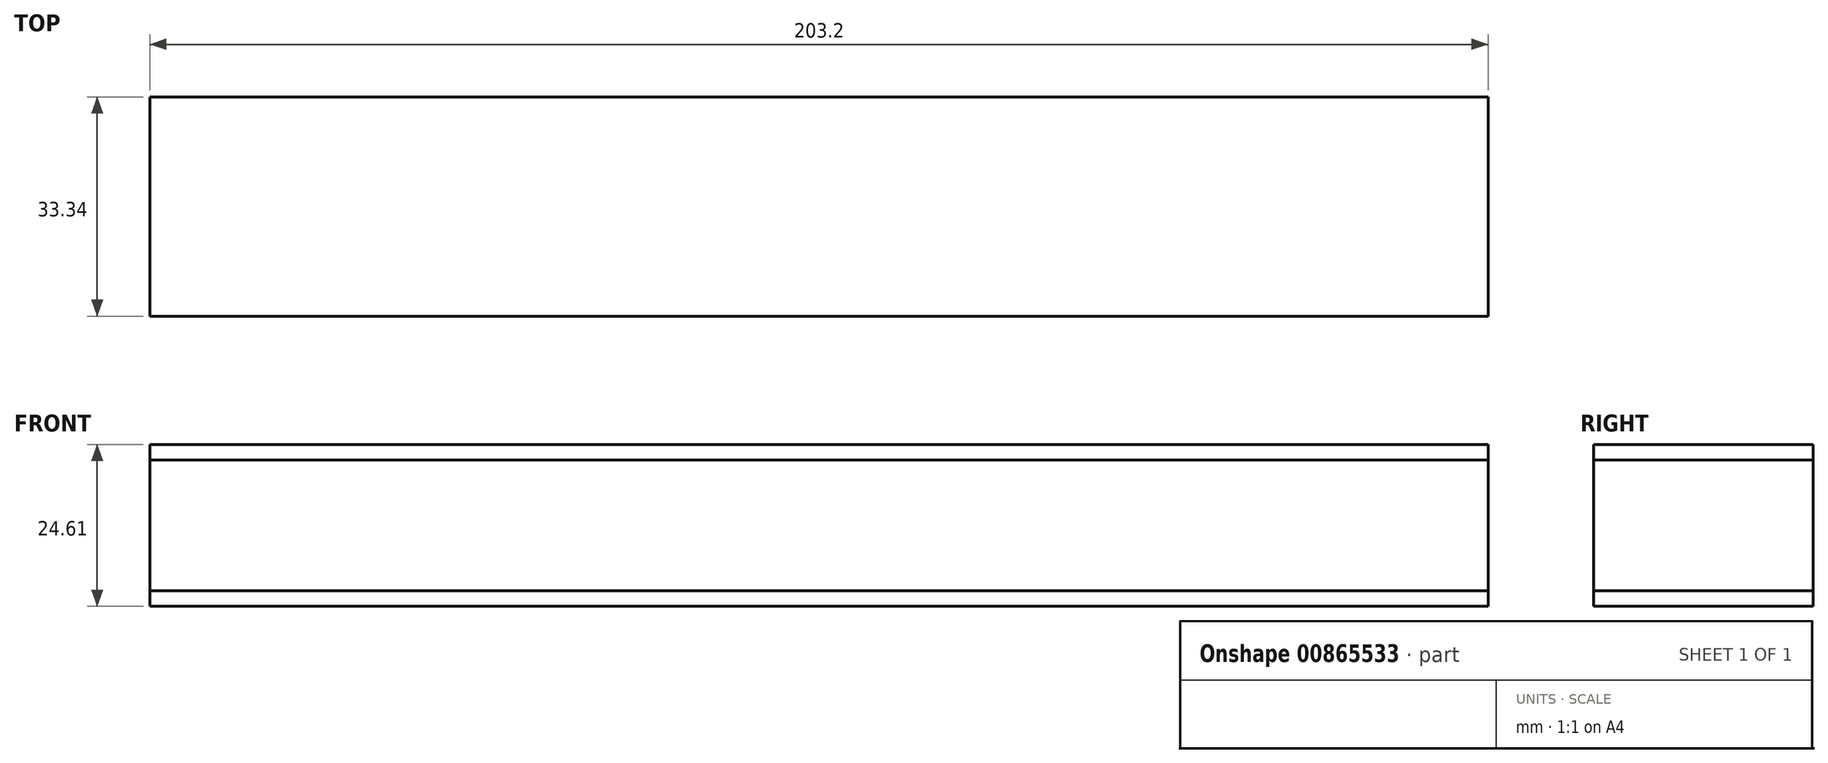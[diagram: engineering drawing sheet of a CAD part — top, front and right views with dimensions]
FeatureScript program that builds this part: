
annotation { "Feature Type Name" : "Feature", "Feature Type Description" : "" }
export const myFeature = defineFeature(function(context is Context, id is Id, definition is map)
    precondition{}
    {
        {
            var Q0;
            Q0=qCreatedBy(makeId("Front.planeOp"),FACE);
            var sketch = newSketch(context, id + "F0", { "sketchPlane" : qUnion([Q0])});
            skLineSegment(sketch, "E0.bottom", {"start": v(0, 0) * mm, "end": v(203.2, 0) * mm});
            skLineSegment(sketch, "E0.top", {"start": v(0, 19.84) * mm, "end": v(203.2, 19.84) * mm});
            skLineSegment(sketch, "E0.left", {"start": v(0, 0) * mm, "end": v(0, 19.84) * mm});
            skLineSegment(sketch, "E0.right", {"start": v(203.2, 0) * mm, "end": v(203.2, 19.84) * mm});
            skSolve(sketch);
        }
        {
            var Q0;
            Q0=makeQuery(id+"F0.imprint","IMPRINT",FACE,{"disambiguationData":[TD([[makeQuery(id+"F0.imprint","IMPRINT",EDGE,{"derivedFrom":sQuery(id+"F0.wireOp",EDGE,"E0.top")}),-1.0]])]});
            extrude(context, id + "F1", {"entities" : qUnion([Q0]), "depth" : 33.34 * mm, "offsetDistance" : 25.4 * mm});
        }
        {
            var Q0;
            Q0=qCreatedBy(makeId("Front.planeOp"),FACE);
            var sketch = newSketch(context, id + "F2", { "sketchPlane" : qUnion([Q0])});
            skLineSegment(sketch, "E1.bottom", {"start": v(0, 19.84) * mm, "end": v(203.2, 19.84) * mm});
            skLineSegment(sketch, "E1.top", {"start": v(0, 22.23) * mm, "end": v(203.2, 22.23) * mm});
            skLineSegment(sketch, "E1.left", {"start": v(0, 19.84) * mm, "end": v(0, 22.23) * mm});
            skLineSegment(sketch, "E1.right", {"start": v(203.2, 19.84) * mm, "end": v(203.2, 22.23) * mm});
            skLineSegment(sketch, "E2", {"start": v(0, 9.92) * mm, "end": v(203.53, 9.92) * mm, "construction": true});
            skLineSegment(sketch, "E3.MirrorCS", {"start": v(0, 0) * mm, "end": v(203.2, 0) * mm});
            skLineSegment(sketch, "E4.MirrorCS", {"start": v(0, -2.38) * mm, "end": v(203.2, -2.38) * mm});
            skLineSegment(sketch, "E5.MirrorCS", {"start": v(0, 0) * mm, "end": v(0, -2.38) * mm});
            skLineSegment(sketch, "E6.MirrorCS", {"start": v(203.2, 0) * mm, "end": v(203.2, -2.38) * mm});
            skSolve(sketch);
        }
        {
            var Q0;
            Q0=makeQuery(id+"F2.imprint","IMPRINT",FACE,{"disambiguationData":[TD([[makeQuery(id+"F2.imprint","IMPRINT",EDGE,{"derivedFrom":sQuery(id+"F2.wireOp",EDGE,"E1.bottom")}),1.0]])]});
            var Q1;
            Q1=makeQuery(id+"F2.imprint","IMPRINT",FACE,{"disambiguationData":[TD([[makeQuery(id+"F2.imprint","IMPRINT",EDGE,{"derivedFrom":sQuery(id+"F2.wireOp",EDGE,"E3.MirrorCS")}),-1.0]])]});
            extrude(context, id + "F3", {"entities" : qUnion([Q0, Q1]), "depth" : 33.34 * mm, "offsetDistance" : 25.4 * mm});
        }
    });
